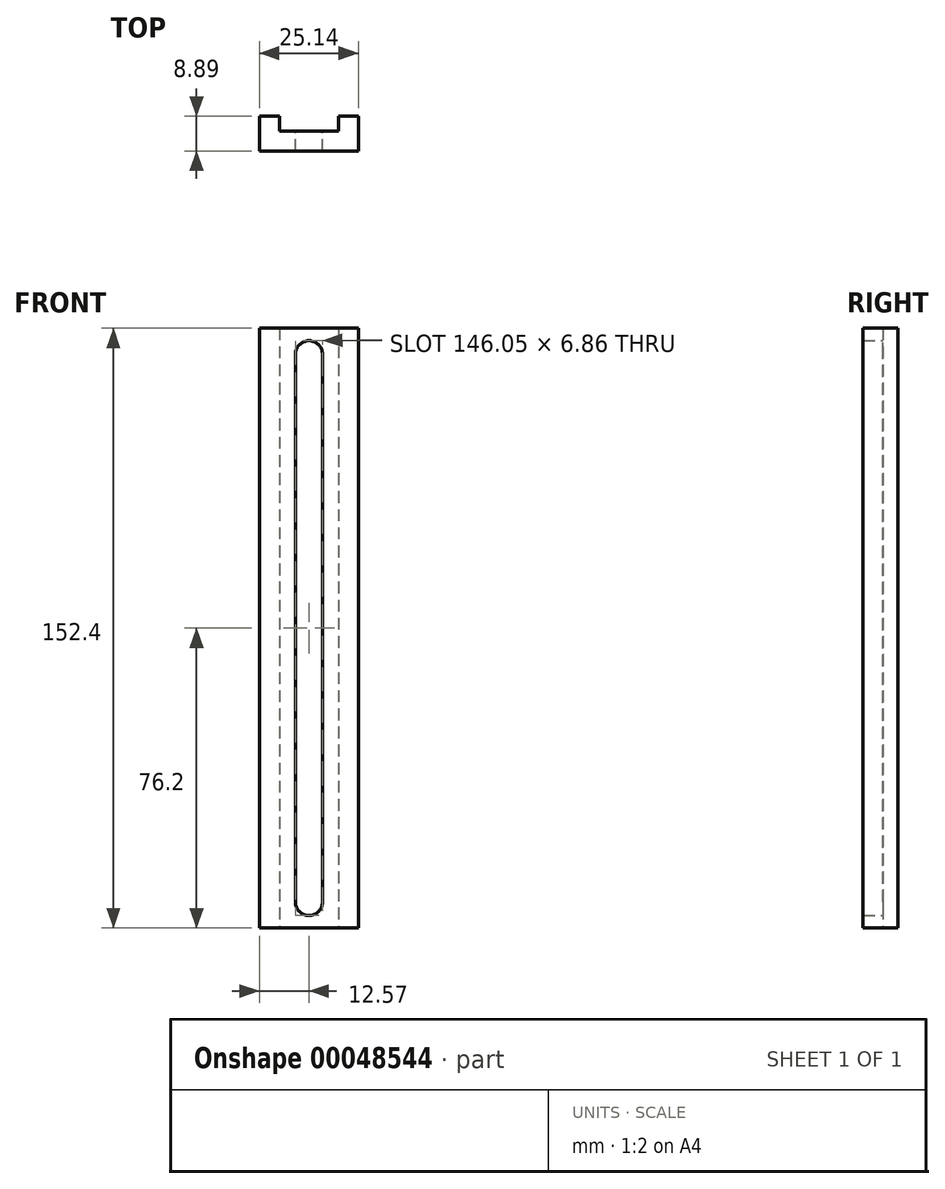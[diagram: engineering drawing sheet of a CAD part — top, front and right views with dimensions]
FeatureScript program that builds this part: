
annotation { "Feature Type Name" : "Feature", "Feature Type Description" : "" }
export const myFeature = defineFeature(function(context is Context, id is Id, definition is map)
    precondition{}
    {
        {
            var Q0;
            Q0=qCreatedBy(makeId("Front.planeOp"),FACE);
            var sketch = newSketch(context, id + "F0", { "sketchPlane" : qUnion([Q0])});
            skLineSegment(sketch, "E0.rect.bottom", {"start": v(-12.57, -76.2) * mm, "end": v(12.57, -76.2) * mm});
            skLineSegment(sketch, "E0.rect.top", {"start": v(-12.57, 76.2) * mm, "end": v(12.57, 76.2) * mm});
            skLineSegment(sketch, "E0.rect.left", {"start": v(-12.57, -76.2) * mm, "end": v(-12.57, 76.2) * mm});
            skLineSegment(sketch, "E0.rect.right", {"start": v(12.57, -76.2) * mm, "end": v(12.57, 76.2) * mm});
            skPoint(sketch, "E0.rect.middle", {"position": v(0, 0) * mm});
            skLineSegment(sketch, "E1.rect.bottom", {"start": v(-3.43, -73.03) * mm, "end": v(3.43, -73.03) * mm});
            skLineSegment(sketch, "E1.rect.top", {"start": v(-3.43, 73.03) * mm, "end": v(3.43, 73.03) * mm});
            skLineSegment(sketch, "E1.rect.left", {"start": v(-3.43, -73.03) * mm, "end": v(-3.43, 73.03) * mm});
            skLineSegment(sketch, "E1.rect.right", {"start": v(3.43, -73.03) * mm, "end": v(3.43, 73.03) * mm});
            skLineSegment(sketch, "E2.bottom", {"start": v(-12.57, 76.2) * mm, "end": v(-7.5, 76.2) * mm});
            skLineSegment(sketch, "E2.top", {"start": v(-12.57, -76.2) * mm, "end": v(-7.5, -76.2) * mm});
            skLineSegment(sketch, "E2.left", {"start": v(-12.57, 76.2) * mm, "end": v(-12.57, -76.2) * mm});
            skLineSegment(sketch, "E2.right", {"start": v(-7.5, 76.2) * mm, "end": v(-7.5, -76.2) * mm});
            skLineSegment(sketch, "E3.bottom", {"start": v(12.57, 76.2) * mm, "end": v(7.5, 76.2) * mm});
            skLineSegment(sketch, "E3.top", {"start": v(12.57, -76.2) * mm, "end": v(7.5, -76.2) * mm});
            skLineSegment(sketch, "E3.left", {"start": v(12.57, 76.2) * mm, "end": v(12.57, -76.2) * mm});
            skLineSegment(sketch, "E3.right", {"start": v(7.5, 76.2) * mm, "end": v(7.5, -76.2) * mm});
            skSolve(sketch);
        }
        {
            var Q0;
            Q0=makeQuery(id+"F0.imprint","IMPRINT",FACE,{"disambiguationData":[TD([[makeQuery(id+"F0.imprint","IMPRINT",EDGE,{"derivedFrom":sQuery(id+"F0.wireOp",EDGE,"E1.rect.bottom")}),-1.0]])]});
            var Q1;
            {var subQ2=sQuery(id+"F0.wireOp",EDGE,"E0.rect.left");Q1=makeQuery(id+"F0.imprint","IMPRINT",FACE,{"disambiguationData":[TD([[makeQuery(id+"F0.imprint","IMPRINT",EDGE,{"derivedFrom":subQ2}),-1.0]])]});}
            var Q2;
            {var subQ0=sQuery(id+"F0.wireOp",EDGE,"E0.rect.right");Q2=makeQuery(id+"F0.imprint","IMPRINT",FACE,{"disambiguationData":[TD([[makeQuery(id+"F0.imprint","IMPRINT",EDGE,{"derivedFrom":subQ0}),1.0]])]});}
            extrude(context, id + "F1", {"entities" : qUnion([Q0, Q1, Q2]), "depth" : 5.08 * mm});
        }
        {
            var Q0;
            Q0=makeQuery(id+"F1.opExtrude","SWEPT_EDGE",EDGE,{"disambiguationData":[OSD([sQuery(id+"F0.wireOp",EDGE,"E1.rect.top"),sQuery(id+"F0.wireOp",EDGE,"E1.rect.right")])]});
            var Q1;
            Q1=makeQuery(id+"F1.opExtrude","SWEPT_EDGE",EDGE,{"disambiguationData":[OSD([sQuery(id+"F0.wireOp",EDGE,"E1.rect.top"),sQuery(id+"F0.wireOp",EDGE,"E1.rect.left")])]});
            var Q2;
            Q2=makeQuery(id+"F1.opExtrude","SWEPT_EDGE",EDGE,{"disambiguationData":[OSD([sQuery(id+"F0.wireOp",EDGE,"E1.rect.bottom"),sQuery(id+"F0.wireOp",EDGE,"E1.rect.left")])]});
            var Q3;
            Q3=makeQuery(id+"F1.opExtrude","SWEPT_EDGE",EDGE,{"disambiguationData":[OSD([sQuery(id+"F0.wireOp",EDGE,"E1.rect.bottom"),sQuery(id+"F0.wireOp",EDGE,"E1.rect.right")])]});
            fillet(context, id + "F2", {"entities" : qUnion([Q0, Q1, Q2, Q3]), "radius" : 3.43 * mm, "tangentPropagation" : true, "allowEdgeOverflow" : false});
        }
        {
            var Q0;
            {var subQ0=sQuery(id+"F0.wireOp",EDGE,"E0.rect.right");Q0=makeQuery(id+"F0.imprint","IMPRINT",FACE,{"disambiguationData":[TD([[makeQuery(id+"F0.imprint","IMPRINT",EDGE,{"derivedFrom":subQ0}),1.0]])]});}
            var Q1;
            {var subQ2=sQuery(id+"F0.wireOp",EDGE,"E0.rect.left");Q1=makeQuery(id+"F0.imprint","IMPRINT",FACE,{"disambiguationData":[TD([[makeQuery(id+"F0.imprint","IMPRINT",EDGE,{"derivedFrom":subQ2}),-1.0]])]});}
            extrude(context, id + "F3", {"entities" : qUnion([Q0, Q1]), "operationType" : NewBodyOperationType.ADD, "oppositeDirection" : true, "depth" : 3.8 * mm});
        }
    });
